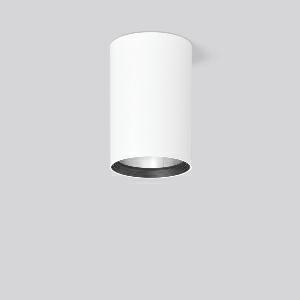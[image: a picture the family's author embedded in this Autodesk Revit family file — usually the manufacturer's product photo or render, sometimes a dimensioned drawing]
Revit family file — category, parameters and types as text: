
# Revit family: heledon_maxi_a_931219_002_2_c3d0
name_source: partatom
category: Lighting Fixtures
units: mm (PartAtom-declared; Revit-internal decimal feet)

## family parameters
Cut with Voids When Loaded = No
Host = Face
Light Source = No
Part Type = Normal
Room Calculation Point = No
Round Connector Dimension = Use Diameter
Shared = No

## types (1)
- HELEDON maxi A (1 x LED Modul 927, 3050 lm, 2700)
    Apparent Load = 25 VA
    Approval mark = CE
    CIE Flux Codes = 97 100 100 100 100
    Color Rendering = 92
    Color Temperature = 2700
    Default Elevation = 1800 mm
    Description = Series: HELEDON maxi
Cylindrical surface-mounted downlight. Housing: die-cast aluminium, powder-coated. Internal ceiling frame polycarbonate with bayonet mounting. Black plastic ring and recessed LED to prevent glare from the side. Optical assembly with reflector made of MIRO-Silver with 98% total light reflection for outstanding efficiency - can be changed without tools. Best colour rendering index Ra>90. Suitable for Ceiling mounting. Easy installation with a separate ceiling frame with bayonet mounting and plug connection. Driver integrated. Connected via plug-in connector. High quality converter without flickering and stroboscopic effect. The following accessories can be mounted without use of tools: interchangeable lenses, decorative glasses, honeycomb louvre, clear and frosted diffusers, white interchangeable plastic ring. 
Colour: traffic white, matt (RAL 9016)
Diameter: 123 mm
Height: 183 mm
Lamp: LED
Socket: without socket
Colour temperature: 2700K
Colour rendering index (CRI): 92
System power: 25 W
Rated luminous flux: 3050 lm
Luminous efficiency: 122 lm/W
Control gear: Regulated power supply
Protection class: I
Type of protection: IP 20
    Height = 183 mm
    Lamp = 1 x LED Modul 927
    Lamp Light Flux = 3050 lm
    Lamp count = 1
    Length = 123 mm
    Lifetime = 50000 h
    Luminous efficacy = 122 lm/W
    Manufacturer = RZB
    ModVariant = No
    Model = 931219.002.2
    Mounting Place = Ceiling
    Mounting Type = Surface mounted
    Number of Poles = 1
    OnlyDefault = Yes
    Power Factor = 1
    Product Name = HELEDON maxi A
    Product group = Surface mounted downlights
    ProductGroupID = 302
    Protection Class = Protection class I
    Protection Degree = IP 20
    RLX_Detail_Level = 1
    RLX_Emergency_Light_Flux = 0 lm
    RLX_Emergency_Type = 0
    RLX_Emergency_Type_DB = No
    RlxData = <blob elided: 97657 chars, md5=8929f800>
    Socket = socket
    Standby Power = 0 W
    System Light Flux = 3050 lm
    System Power = 25 W
    Type Comments = Product without accessories
    Type Image = 931192.002.jpg
    URL = http://relux.com
    VarID = ---
    Voltage = 230 V
    Voltage Range = 220-240 V
    Weight = 0.00 kg
    Width = 0 mm  [stored 0 ft]

note: [stored X ft] marks values corroborated as IEEE doubles in the binary element streams (Revit-internal decimal feet)

## geometry (parser evidence)
native form markers: Blend x4, Sweep x10
no freeform markers — native parametric forms only
